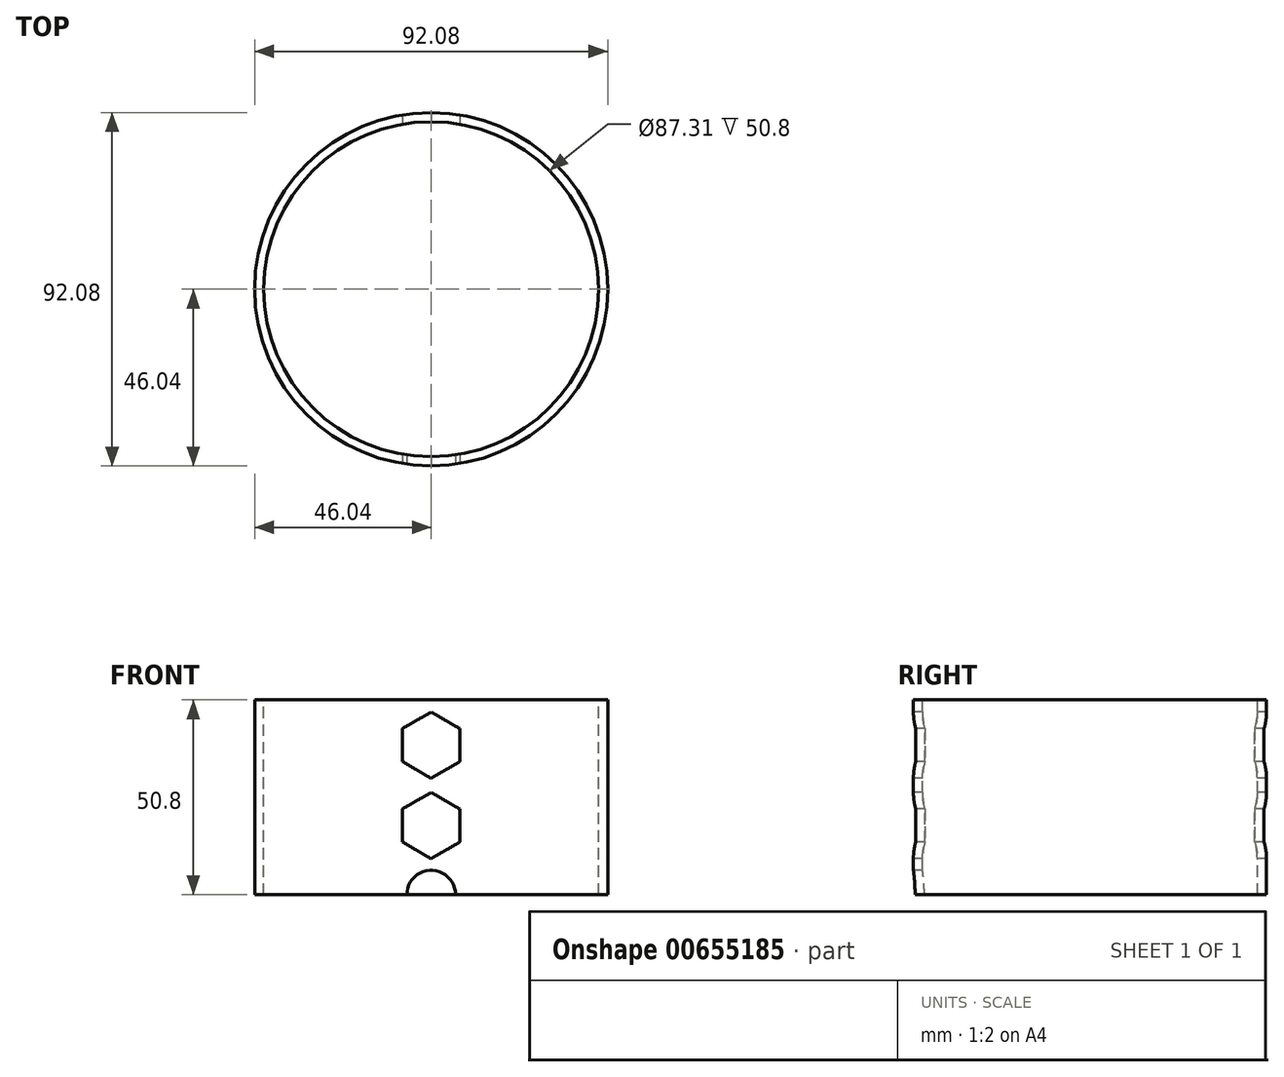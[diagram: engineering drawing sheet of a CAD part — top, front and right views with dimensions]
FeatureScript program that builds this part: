
annotation { "Feature Type Name" : "Feature", "Feature Type Description" : "" }
export const myFeature = defineFeature(function(context is Context, id is Id, definition is map)
    precondition{}
    {
        {
            var Q0;
            Q0=qCreatedBy(makeId("Top.planeOp"),FACE);
            var sketch = newSketch(context, id + "F0", { "sketchPlane" : qUnion([Q0])});
            skCircle(sketch, "E0", {"center": v(0, 0) * mm, "radius": 46.04 * mm});
            skCircle(sketch, "E1", {"center": v(0, 0) * mm, "radius": 43.66 * mm});
            skSolve(sketch);
        }
        {
            var Q0;
            Q0 = qSketchRegion(id + "F0", true);
            extrude(context, id + "F1", {"entities" : qUnion([Q0]), "oppositeDirection" : true, "depth" : 50.8 * mm, "offsetDistance" : 25.4 * mm});
        }
        {
            var Q0;
            Q0=qCreatedBy(makeId("Front.planeOp"),FACE);
            cPlane(context, id + "F2", {"entities" : qUnion([Q0]), "cplaneType" : CPlaneType.OFFSET, "offset" : 46.48 * mm, "width" : 152.4 * mm, "height" : 152.4 * mm});
        }
        {
            var Q0;
            Q0=qCreatedBy(id+"F2.planeOp",FACE);
            var sketch = newSketch(context, id + "F3", { "sketchPlane" : qUnion([Q0])});
            skCircle(sketch, "E2", {"center": v(0, -50.8) * mm, "radius": 6.35 * mm});
            skSolve(sketch);
        }
        {
            var Q0;
            Q0 = qSketchRegion(id + "F3", true);
            extrude(context, id + "F4", {"entities" : qUnion([Q0]), "operationType" : NewBodyOperationType.REMOVE, "oppositeDirection" : true, "depth" : 5.6 * mm, "offsetDistance" : 25.4 * mm});
        }
        {
            var Q0;
            Q0=qCreatedBy(id+"F2.planeOp",FACE);
            var sketch = newSketch(context, id + "F5", { "sketchPlane" : qUnion([Q0])});
            skCircle(sketch, "E3.cCircle", {"center": v(0, -11.8) * mm, "radius": 7.47 * mm, "construction": true});
            skLineSegment(sketch, "E3.0", {"start": v(7.46, -16.15) * mm, "end": v(-0.03, -20.44) * mm});
            skLineSegment(sketch, "E3.1", {"start": v(-0.03, -20.44) * mm, "end": v(-7.5, -16.1) * mm});
            skLineSegment(sketch, "E3.2", {"start": v(-7.5, -16.1) * mm, "end": v(-7.46, -7.46) * mm});
            skLineSegment(sketch, "E3.3", {"start": v(-7.46, -7.46) * mm, "end": v(0.03, -3.17) * mm});
            skLineSegment(sketch, "E3.4", {"start": v(0.03, -3.17) * mm, "end": v(7.5, -7.52) * mm});
            skLineSegment(sketch, "E3.5", {"start": v(7.5, -7.52) * mm, "end": v(7.46, -16.15) * mm});
            skPoint(sketch, "E3.0.midPoint", {"position": v(3.71, -18.3) * mm});
            skCircle(sketch, "E4.0.1.0", {"center": v(0, -32.76) * mm, "radius": 7.47 * mm, "construction": true});
            skPoint(sketch, "E4.0.1.1", {"position": v(3.71, -39.25) * mm});
            skLineSegment(sketch, "E4.0.1.2", {"start": v(7.5, -28.47) * mm, "end": v(7.46, -37.1) * mm});
            skLineSegment(sketch, "E4.0.1.3", {"start": v(0.03, -24.13) * mm, "end": v(7.5, -28.47) * mm});
            skLineSegment(sketch, "E4.0.1.4", {"start": v(-7.46, -28.42) * mm, "end": v(0.03, -24.13) * mm});
            skLineSegment(sketch, "E4.0.1.5", {"start": v(-7.5, -37.05) * mm, "end": v(-7.46, -28.42) * mm});
            skLineSegment(sketch, "E4.0.1.6", {"start": v(-0.03, -41.4) * mm, "end": v(-7.5, -37.05) * mm});
            skLineSegment(sketch, "E4.0.1.7", {"start": v(7.46, -37.1) * mm, "end": v(-0.03, -41.4) * mm});
            skLineSegment(sketch, "E4.direction1", {"start": v(-7.5, -16.1) * mm, "end": v(17.9, -16.1) * mm, "construction": true});
            skLineSegment(sketch, "E4.direction2", {"start": v(-7.5, -16.1) * mm, "end": v(-7.5, -37.05) * mm, "construction": true});
            skSolve(sketch);
        }
        {
            var Q0;
            Q0 = qSketchRegion(id + "F5", true);
            extrude(context, id + "F6", {"entities" : qUnion([Q0]), "operationType" : NewBodyOperationType.REMOVE, "endBound" : BoundingType.THROUGH_ALL, "oppositeDirection" : true, "depth" : 6.35 * mm, "offsetDistance" : 25.4 * mm});
        }
    });
